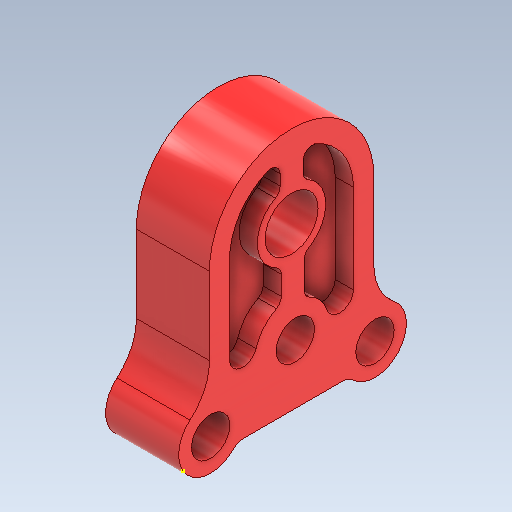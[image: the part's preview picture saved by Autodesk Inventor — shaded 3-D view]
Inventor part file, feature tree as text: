
AUTODESK INVENTOR PART (.ipt)
format: ipt  version: 2021 (Build 250183000, 183)  size: 294,400 bytes
history: native  units: in
note: dims shown in document units (in); Inventor stores cm internally (conversion verified against a paired STEP export)
features: sketch x2, extrude x2
ambient origin geometry x8: Origin, YZ Plane, XZ Plane, XY Plane, X Axis, Y Axis, Z Axis, Center Point
bodies: Solid1 (feature_tree)
feature tree (4):
  sketch  "Sketch1"  dims[d36=2.3622in d37=1.6535in]
  extrude  "Extrusion1"  Depth=2.3622in
  sketch  "Sketch2"  dims[d38=1.378in d40=1.6535in d41=1.7717in d42=1.7717in d44=1.1417in d45=0.9055in d50=3.5433in d51=0.5906in d52=0.5906in d53=0.5906in d54=7.0866in d55=2.3622in d56=1.5748in d57=1.5748in d58=0.0in d59=0.0in d60=0.7874in d61=0.7874in d62=0.0in d63=0.0in d64=2.2835in d66=0.9843in d68=0.3937in d69=1.4764in d75=0.8661in d79=0.3937in d78=0.0197in d80=0.0197in d81=0.0344in]
  extrude  "Extrusion2"  Depth=0.3937in
